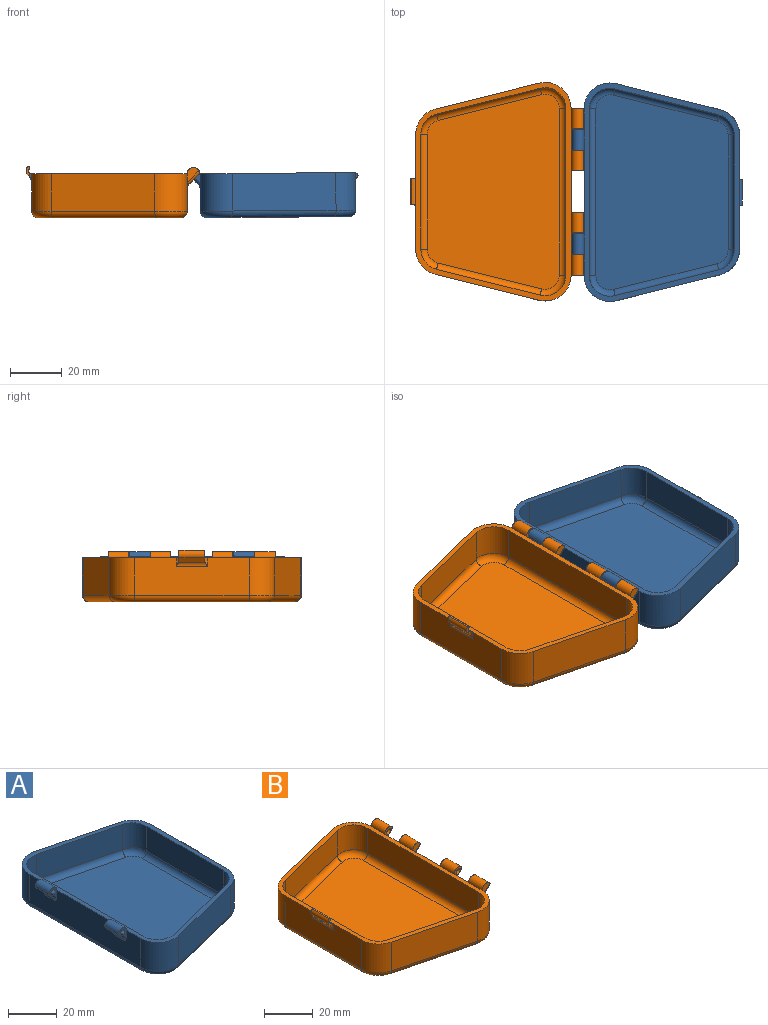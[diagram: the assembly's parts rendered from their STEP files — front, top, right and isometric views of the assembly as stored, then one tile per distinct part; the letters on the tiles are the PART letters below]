
ASSEMBLY  parts=2 mates=1
PART A: 70 faces, bbox 66.2x86x19.4 mm
  f0: plane 64.38x14.5mm, normal (-1,0,0), area 843.3mm2, adj f1,f7,f17,f19,f22,f23,f24,f34
  f1: cylinder r=10mm len=14.5mm, axis (0,0,1), area 263.3mm2, adj f0,f2,f17,f45
  f2: plane 40x14.5mm, normal (0.24,-0.97,0), area 597.9mm2, adj f1,f3,f17,f44
  f3: cylinder r=10mm len=14.5mm, axis (0,0,1), area 192.2mm2, adj f2,f4,f17,f46
  f4: plane 44.38x14.5mm, normal (1,0,0), area 623.6mm2, adj f3,f5,f17,f31,f32,f33,f48
  f5: cylinder r=10mm len=14.5mm, axis (0,0,1), area 192.2mm2, adj f4,f6,f17,f50
  f6: plane 40x14.5mm, normal (0.24,0.97,0), area 597.9mm2, adj f5,f7,f17,f51
  f7: cylinder r=10mm len=14.5mm, axis (0,0,1), area 263.3mm2, adj f0,f6,f17,f49
  f8: plane 79.38x55mm, normal (0,0,-1), area 3786.3mm2, adj f44,f45,f46,f47,f48,f49,f50,f51
  f9: plane 64.38x12.5mm, normal (1,0,0), area 804.8mm2, adj f10,f16,f17,f39
  f10: cylinder r=8mm len=12.5mm, axis (0,0,-1), area 181.6mm2, adj f9,f11,f17,f37
  f11: plane 40x12.5mm, normal (-0.24,-0.97,0), area 515.4mm2, adj f10,f12,f17,f36
  f12: cylinder r=8mm len=12.5mm, axis (0,0,-1), area 132.6mm2, adj f11,f13,f17,f38
  f13: plane 44.38x12.5mm, normal (-1,0,0), area 554.8mm2, adj f12,f14,f17,f40
  f14: cylinder r=8mm len=12.5mm, axis (0,0,-1), area 132.6mm2, adj f13,f15,f17,f42
  f15: plane 40x12.5mm, normal (-0.24,0.97,0), area 515.4mm2, adj f14,f16,f17,f43
  f16: cylinder r=8mm len=12.5mm, axis (0,0,-1), area 181.6mm2, adj f9,f15,f17,f41
  f17: plane 84.38x60mm, normal (0,0,1), area 495.6mm2, adj f0,f1,f2,f3,f4,f5,f6,f7
  f18: plane 75.38x51mm, normal (0,0,1), area 3322.2mm2, adj f36,f37,f38,f39,f40,f41,f42,f43
  f19: plane 5.79x4.52mm, normal (0,-1,0), area 10mm2, adj f0,f20,f27,f66,f68,f69
  f20: cylinder r=2.4mm len=8.05mm, axis (0,1,0), area 55.5mm2, adj f17,f19,f22,f64,f65,f66
  f21: plane 6.49x3.73mm, normal (-0.71,0,-0.71), area 32.3mm2, adj f35,f62,f63,f64,f65,f66,f67,f68
  f22: plane 5.79x4.52mm, normal (0,1,0), area 10mm2, adj f0,f20,f28,f61,f62,f64
  f23: plane 5.79x4.52mm, normal (0,1,0), area 10mm2, adj f0,f25,f29,f57,f59,f60
  f24: plane 5.79x4.52mm, normal (0,-1,0), area 10mm2, adj f0,f25,f30,f52,f53,f55
  f25: cylinder r=2.4mm len=8.05mm, axis (0,-1,0), area 55.5mm2, adj f17,f23,f24,f55,f56,f57
  f26: plane 6.49x3.73mm, normal (-0.71,0,-0.71), area 32.3mm2, adj f34,f53,f54,f55,f56,f57,f58,f59
  f27: cone r=1.25mm half-angle=45deg, axis (0,1,0), area 6.9mm2, adj f19,f67
  f28: cone r=1.25mm half-angle=45deg, axis (0,-1,0), area 6.9mm2, adj f22,f63
  f29: cone r=1.25mm half-angle=45deg, axis (0,-1,0), area 6.9mm2, adj f23,f58
  f30: cone r=1.25mm half-angle=45deg, axis (0,1,0), area 6.9mm2, adj f24,f54
  f31: cylinder r=1mm len=10mm, axis (0,1,0), area 31.4mm2, adj f4,f32,f33
  f32: plane 2x1mm, normal (0,-1,0), area 1.6mm2, adj f4,f31
  f33: plane 2x1mm, normal (0,1,0), area 1.6mm2, adj f4,f31
  f34: cylinder r=2.5mm len=6.05mm, axis (0,-1,0), area 11.9mm2, adj f0,f26,f52,f60
  f35: cylinder r=2.5mm len=6.05mm, axis (0,-1,0), area 11.9mm2, adj f0,f21,f61,f69
  f36: cylinder r=2.5mm len=40.61mm, axis (0.97,-0.24,0), area 161.9mm2, adj f11,f18,f37,f38
  f37: torus R=5.5mm, axis (0,0,1), area 50.6mm2, adj f10,f18,f36,f39
  f38: torus R=5.5mm, axis (0,0,1), area 36.9mm2, adj f12,f18,f36,f40
  f39: cylinder r=2.5mm len=64.38mm, axis (0,1,0), area 252.8mm2, adj f9,f18,f37,f41
  f40: cylinder r=2.5mm len=44.38mm, axis (0,-1,0), area 174.3mm2, adj f13,f18,f38,f42
  f41: torus R=5.5mm, axis (0,0,1), area 50.6mm2, adj f16,f18,f39,f43
  f42: torus R=5.5mm, axis (0,0,1), area 36.9mm2, adj f14,f18,f40,f43
  f43: cylinder r=2.5mm len=40.61mm, axis (-0.97,-0.24,0), area 161.9mm2, adj f15,f18,f41,f42
  f44: cylinder r=2.5mm len=40.61mm, axis (-0.97,-0.24,0), area 161.9mm2, adj f2,f8,f45,f46
  f45: torus R=7.5mm, axis (0,0,1), area 64.8mm2, adj f1,f8,f44,f47
  f46: torus R=7.5mm, axis (0,0,1), area 47.3mm2, adj f3,f8,f44,f48
  f47: cylinder r=2.5mm len=64.38mm, axis (0,1,0), area 252.8mm2, adj f0,f8,f45,f49
  f48: cylinder r=2.5mm len=44.38mm, axis (0,-1,0), area 174.3mm2, adj f4,f8,f46,f50
  f49: torus R=7.5mm, axis (0,0,1), area 64.8mm2, adj f7,f8,f47,f51
  f50: torus R=7.5mm, axis (0,0,1), area 47.3mm2, adj f5,f8,f48,f51
  f51: cylinder r=2.5mm len=40.61mm, axis (0.97,-0.24,0), area 161.9mm2, adj f6,f8,f49,f50
  f52: torus R=3.5mm, axis (0,1,0), area 1.5mm2, adj f0,f24,f34,f53
  f53: cylinder r=1mm len=2.86mm, axis (-0.71,0,0.71), area 4.8mm2, adj f24,f26,f52,f54
  f54: bspline ~2.24x2.24mm, area 2.4mm2, adj f26,f30,f53,f55
  f55: cylinder r=1mm len=1.52mm, axis (-0.71,0,0.71), area 1.1mm2, adj f24,f25,f26,f54,f56
  f56: cylinder r=1mm len=7.78mm, axis (0,-1,0), area 7.3mm2, adj f25,f26,f55,f57
  f57: cylinder r=1mm len=1.52mm, axis (0.71,0,-0.71), area 1.1mm2, adj f23,f25,f26,f56,f58
  f58: bspline ~2.42x2.38mm, area 2.4mm2, adj f26,f29,f57,f59
  f59: cylinder r=1mm len=2.86mm, axis (0.71,0,-0.71), area 4.8mm2, adj f23,f26,f58,f60
  f60: torus R=3.5mm, axis (0,1,0), area 1.5mm2, adj f0,f23,f34,f59
  f61: torus R=3.5mm, axis (0,-1,0), area 1.5mm2, adj f0,f22,f35,f62
  f62: cylinder r=1mm len=2.86mm, axis (0.71,0,-0.71), area 4.8mm2, adj f21,f22,f61,f63
  f63: bspline ~2.24x2.24mm, area 2.4mm2, adj f21,f28,f62,f64
  f64: cylinder r=1mm len=1.52mm, axis (0.71,0,-0.71), area 1.1mm2, adj f20,f21,f22,f63,f65
  f65: cylinder r=1mm len=7.78mm, axis (0,1,0), area 7.3mm2, adj f20,f21,f64,f66
  f66: cylinder r=1mm len=1.52mm, axis (-0.71,0,0.71), area 1.1mm2, adj f19,f20,f21,f65,f67
  f67: bspline ~2.24x2.24mm, area 2.4mm2, adj f21,f27,f66,f68
  f68: cylinder r=1mm len=2.86mm, axis (-0.71,0,0.71), area 4.8mm2, adj f19,f21,f67,f69
  f69: torus R=3.5mm, axis (0,-1,0), area 1.5mm2, adj f0,f19,f35,f68
PART B: 88 faces, bbox 67.5x86.1x19.9 mm
  f0: plane 64.39x14.5mm, normal (1,0,0), area 754mm2, adj f1,f7,f17,f19,f23,f26,f27,f28
  f1: cylinder r=10mm len=14.5mm, axis (0,0,1), area 264.9mm2, adj f0,f2,f17,f32,f61,f66
  f2: plane 40x14.5mm, normal (-0.24,0.97,0), area 597.9mm2, adj f1,f3,f17,f59
  f3: cylinder r=10mm len=14.5mm, axis (0,0,1), area 192.2mm2, adj f2,f4,f17,f58
  f4: plane 44.38x14.5mm, normal (-1,0,0), area 603.7mm2, adj f3,f5,f17,f45,f60,f86,f87
  f5: cylinder r=10mm len=14.5mm, axis (0,0,1), area 192.2mm2, adj f4,f6,f17,f62
  f6: plane 40x14.5mm, normal (-0.24,-0.97,0), area 597.9mm2, adj f5,f7,f17,f64
  f7: cylinder r=10mm len=14.5mm, axis (0,0,1), area 264.9mm2, adj f0,f6,f17,f20,f65,f81
  f8: plane 79.38x55mm, normal (0,0,-1), area 3786.3mm2, adj f58,f59,f60,f61,f62,f63,f64,f65
  f9: cylinder r=8mm len=12.5mm, axis (0,0,-1), area 132.6mm2, adj f10,f16,f17,f56
  f10: plane 44.38x12.5mm, normal (1,0,0), area 554.8mm2, adj f9,f11,f17,f54
  f11: cylinder r=8mm len=12.5mm, axis (0,0,-1), area 132.6mm2, adj f10,f12,f17,f52
  f12: plane 40x12.5mm, normal (0.24,-0.97,0), area 515.4mm2, adj f11,f13,f17,f50
  f13: cylinder r=8mm len=12.5mm, axis (0,0,-1), area 181.6mm2, adj f12,f14,f17,f51
  f14: plane 64.38x12.5mm, normal (-1,0,0), area 804.8mm2, adj f13,f15,f17,f53
  f15: cylinder r=8mm len=12.5mm, axis (0,0,-1), area 181.6mm2, adj f14,f16,f17,f55
  f16: plane 40x12.5mm, normal (0.24,0.97,0), area 515.4mm2, adj f9,f15,f17,f57
  f17: plane 84.38x60mm, normal (0,0,1), area 495.6mm2, adj f0,f1,f2,f3,f4,f5,f6,f7
  f18: plane 75.38x51mm, normal (0,0,1), area 3322.2mm2, adj f50,f51,f52,f53,f54,f55,f56,f57
  f19: plane 5.79x4.52mm, normal (0,1,0), area 9.5mm2, adj f0,f22,f38,f84,f85
  f20: plane 5.79x4.52mm, normal (0,-1,0), area 13.9mm2, adj f7,f22,f81,f82
  f21: plane 5.85x3.73mm, normal (0.71,0,-0.71), area 30.8mm2, adj f49,f82,f83,f84
  f22: cylinder r=2.4mm len=7.85mm, axis (0,1,0), area 54.1mm2, adj f17,f19,f20,f82,f83,f84
  f23: plane 5.79x4.52mm, normal (0,-1,0), area 9.5mm2, adj f0,f25,f37,f79,f80
  f24: plane 5.85x3.73mm, normal (0.71,0,-0.71), area 30.8mm2, adj f48,f77,f78,f79
  f25: cylinder r=2.4mm len=7.85mm, axis (0,1,0), area 54.1mm2, adj f17,f23,f26,f77,f78,f79
  f26: plane 5.79x4.52mm, normal (0,1,0), area 13.9mm2, adj f0,f25,f76,f77
  f27: plane 5.79x4.52mm, normal (0,1,0), area 9.5mm2, adj f0,f30,f36,f74,f75
  f28: plane 5.79x4.52mm, normal (0,-1,0), area 13.9mm2, adj f0,f30,f71,f72
  f29: plane 5.85x3.73mm, normal (0.71,0,-0.71), area 30.8mm2, adj f47,f72,f73,f74
  f30: cylinder r=2.4mm len=7.85mm, axis (0,-1,0), area 54.1mm2, adj f17,f27,f28,f72,f73,f74
  f31: plane 5.79x4.52mm, normal (0,-1,0), area 9.5mm2, adj f0,f34,f35,f69,f70
  f32: plane 5.79x4.52mm, normal (0,1,0), area 13.9mm2, adj f1,f34,f66,f67
  f33: plane 5.85x3.73mm, normal (0.71,0,-0.71), area 30.8mm2, adj f46,f67,f68,f69
  f34: cylinder r=2.4mm len=7.85mm, axis (0,-1,0), area 54.1mm2, adj f17,f31,f32,f67,f68,f69
  f35: cone r=1.73mm half-angle=45deg, axis (0,-1,0), area 7.8mm2, adj f31,f69
  f36: cone r=1.73mm half-angle=45deg, axis (0,1,0), area 7.9mm2, adj f27,f74
  f37: cone r=1.73mm half-angle=45deg, axis (0,-1,0), area 7.8mm2, adj f23,f79
  f38: cone r=1.73mm half-angle=45deg, axis (0,1,0), area 7.9mm2, adj f19,f84
  f39: cylinder r=1.2mm len=12mm, axis (0,1,0), area 29.5mm2, adj f17,f40,f43,f44,f86,f87
  f40: cylinder r=0.5mm len=10mm, axis (0,1,0), area 15.7mm2, adj f39,f41,f43,f44
  f41: cylinder r=2.2mm len=10mm, axis (0,1,0), area 29.9mm2, adj f40,f42,f43,f44
  f42: plane 10.31x1.86mm, normal (-0.8,0,-0.59), area 22.9mm2, adj f41,f43,f44,f45,f86,f87
  f43: plane 4.04x1.5mm, normal (0,-1,0), area 3.4mm2, adj f39,f40,f41,f42,f87
  f44: plane 4.04x1.5mm, normal (0,1,0), area 3.4mm2, adj f39,f40,f41,f42,f86
  f45: cylinder r=2.5mm len=12mm, axis (0,1,0), area 17.7mm2, adj f4,f42,f86,f87
  f46: cylinder r=2.5mm len=5.85mm, axis (0,1,0), area 11.5mm2, adj f0,f33,f66,f70
  f47: cylinder r=2.5mm len=5.85mm, axis (0,1,0), area 11.5mm2, adj f0,f29,f71,f75
  f48: cylinder r=2.5mm len=5.85mm, axis (0,1,0), area 11.5mm2, adj f0,f24,f76,f80
  f49: cylinder r=2.5mm len=5.85mm, axis (0,1,0), area 11.5mm2, adj f0,f21,f81,f85
  f50: cylinder r=2.5mm len=40.61mm, axis (0.97,0.24,0), area 161.9mm2, adj f12,f18,f51,f52
  f51: torus R=5.5mm, axis (0,0,1), area 50.6mm2, adj f13,f18,f50,f53
  f52: torus R=5.5mm, axis (0,0,1), area 36.9mm2, adj f11,f18,f50,f54
  f53: cylinder r=2.5mm len=64.38mm, axis (0,-1,0), area 252.8mm2, adj f14,f18,f51,f55
  f54: cylinder r=2.5mm len=44.38mm, axis (0,1,0), area 174.3mm2, adj f10,f18,f52,f56
  f55: torus R=5.5mm, axis (0,0,1), area 50.6mm2, adj f15,f18,f53,f57
  f56: torus R=5.5mm, axis (0,0,1), area 36.9mm2, adj f9,f18,f54,f57
  f57: cylinder r=2.5mm len=40.61mm, axis (-0.97,0.24,0), area 161.9mm2, adj f16,f18,f55,f56
  f58: torus R=7.5mm, axis (0,0,1), area 47.3mm2, adj f3,f8,f59,f60
  f59: cylinder r=2.5mm len=40.61mm, axis (0.97,0.24,0), area 161.9mm2, adj f2,f8,f58,f61
  f60: cylinder r=2.5mm len=44.38mm, axis (0,1,0), area 174.3mm2, adj f4,f8,f58,f62
  f61: torus R=7.5mm, axis (0,0,1), area 64.8mm2, adj f1,f8,f59,f63
  f62: torus R=7.5mm, axis (0,0,1), area 47.3mm2, adj f5,f8,f60,f64
  f63: cylinder r=2.5mm len=64.38mm, axis (0,-1,0), area 252.8mm2, adj f0,f8,f61,f65
  f64: cylinder r=2.5mm len=40.61mm, axis (-0.97,0.24,0), area 161.9mm2, adj f6,f8,f62,f65
  f65: torus R=7.5mm, axis (0,0,1), area 64.8mm2, adj f7,f8,f63,f64
  f66: torus R=3.5mm, axis (0,1,0), area 1.6mm2, adj f0,f1,f32,f46,f67
  f67: cylinder r=1mm len=5.2mm, axis (0.71,0,0.71), area 9.2mm2, adj f32,f33,f34,f66,f68
  f68: cylinder r=1mm len=7.58mm, axis (0,-1,0), area 7mm2, adj f33,f34,f67,f69
  f69: cylinder r=1mm len=5.2mm, axis (-0.71,0,-0.71), area 8.3mm2, adj f31,f33,f34,f35,f68,f70
  f70: torus R=3.5mm, axis (0,1,0), area 1.5mm2, adj f0,f31,f46,f69
  f71: torus R=3.5mm, axis (0,1,0), area 1.5mm2, adj f0,f28,f47,f72
  f72: cylinder r=1mm len=5.2mm, axis (-0.71,0,-0.71), area 9.2mm2, adj f28,f29,f30,f71,f73
  f73: cylinder r=1mm len=7.58mm, axis (0,-1,0), area 7mm2, adj f29,f30,f72,f74
  f74: cylinder r=1mm len=5.2mm, axis (0.71,0,0.71), area 8.3mm2, adj f27,f29,f30,f36,f73,f75
  f75: torus R=3.5mm, axis (0,1,0), area 1.5mm2, adj f0,f27,f47,f74
  f76: torus R=3.5mm, axis (0,-1,0), area 1.5mm2, adj f0,f26,f48,f77
  f77: cylinder r=1mm len=5.2mm, axis (0.71,0,0.71), area 9.2mm2, adj f24,f25,f26,f76,f78
  f78: cylinder r=1mm len=7.58mm, axis (0,1,0), area 7mm2, adj f24,f25,f77,f79
  f79: cylinder r=1mm len=5.2mm, axis (-0.71,0,-0.71), area 8.3mm2, adj f23,f24,f25,f37,f78,f80
  f80: torus R=3.5mm, axis (0,-1,0), area 1.5mm2, adj f0,f23,f48,f79
  f81: torus R=3.5mm, axis (0,-1,0), area 1.6mm2, adj f0,f7,f20,f49,f82
  f82: cylinder r=1mm len=5.2mm, axis (-0.71,0,-0.71), area 9.2mm2, adj f20,f21,f22,f81,f83
  f83: cylinder r=1mm len=7.58mm, axis (0,1,0), area 7mm2, adj f21,f22,f82,f84
  f84: cylinder r=1mm len=5.2mm, axis (0.71,0,0.71), area 8.3mm2, adj f19,f21,f22,f38,f83,f85
  f85: torus R=3.5mm, axis (0,-1,0), area 1.5mm2, adj f0,f19,f49,f84
  f86: cylinder r=1mm len=3.86mm, axis (0,0,-1), area 3.9mm2, adj f4,f39,f42,f44,f45
  f87: cylinder r=1mm len=3.86mm, axis (0,0,1), area 3.9mm2, adj f4,f39,f42,f43,f45
PLACE A rot(axis=(0,-1,0),0.4deg) t=(-65.91,1.82,-2)mm
PLACE B t=(-66.02,2.02,-2)mm fixed
MATE revolute A.f29 <-> B.f38  axis (0,-1,0) through (-66.02,-18.1,13)mm
